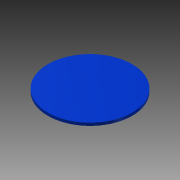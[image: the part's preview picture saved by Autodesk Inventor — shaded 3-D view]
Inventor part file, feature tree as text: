
AUTODESK INVENTOR PART (.ipt)
format: ipt  version: 2015 (Build 190159000, 159)  size: 83,968 bytes
history: native  units: mm
features: extrude x1, sketch x1
ambient origin geometry x8: Origin, YZ Plane, XZ Plane, XY Plane, X Axis, Y Axis, Z Axis, Center Point
bodies: Solid1 (feature_tree)
feature tree (2):
  extrude  "Extrusion1"  Depth=6.0mm TaperAngle=0.0deg
  sketch  "Sketch1"  dims[d0=180.0mm d1=6.0mm d2=0.0mm]
